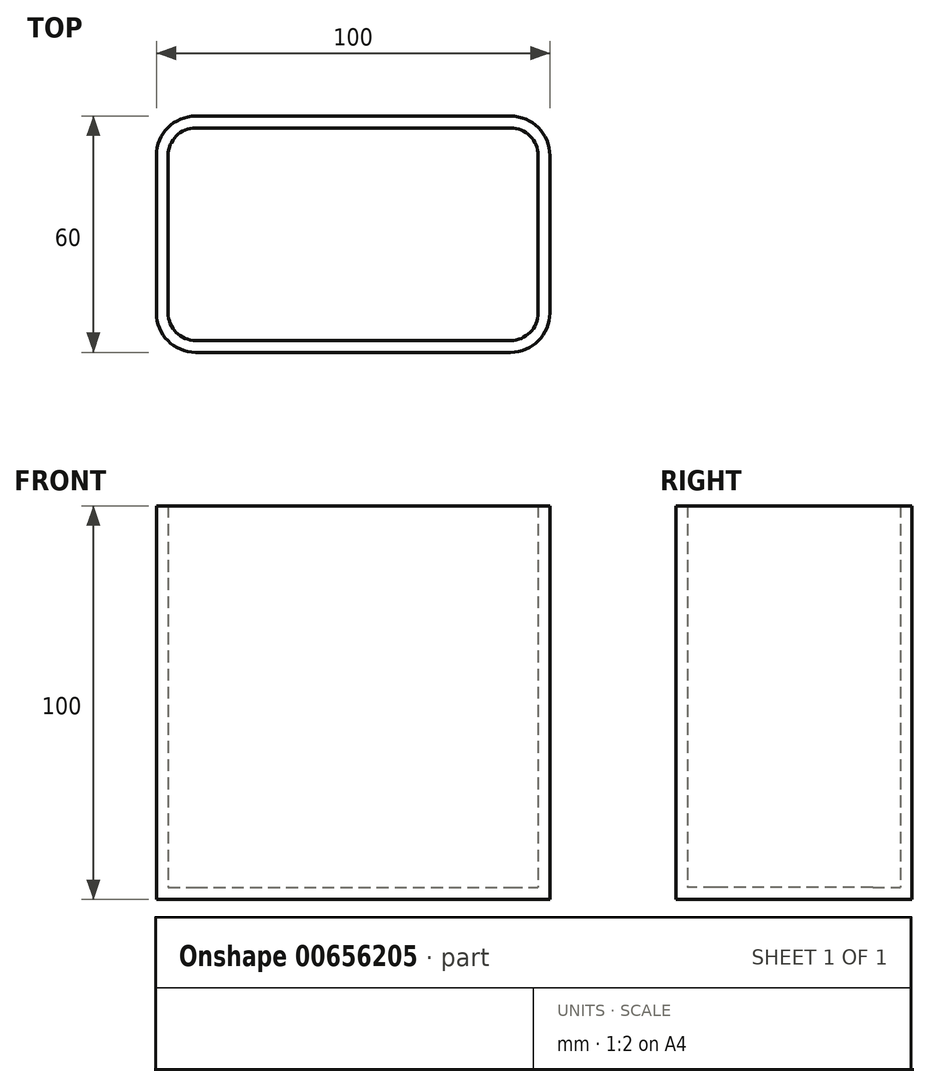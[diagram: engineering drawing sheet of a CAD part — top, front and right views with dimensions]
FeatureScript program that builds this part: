
annotation { "Feature Type Name" : "Feature", "Feature Type Description" : "" }
export const myFeature = defineFeature(function(context is Context, id is Id, definition is map)
    precondition{}
    {
        {
            var Q0;
            Q0=qCreatedBy(makeId("Top.planeOp"),FACE);
            var sketch = newSketch(context, id + "F0", { "sketchPlane" : qUnion([Q0])});
            skLineSegment(sketch, "E0.bottom", {"start": v(40, 30) * mm, "end": v(-40, 30) * mm});
            skLineSegment(sketch, "E0.top", {"start": v(40, -30) * mm, "end": v(-40, -30) * mm});
            skLineSegment(sketch, "E0.left", {"start": v(50, 20) * mm, "end": v(50, -20) * mm});
            skLineSegment(sketch, "E0.right", {"start": v(-50, 20) * mm, "end": v(-50, -20) * mm});
            skPoint(sketch, "E0.middle", {"position": v(0, 0) * mm});
            skPoint(sketch, "E1.visualSharp", {"position": v(-50, 30) * mm});
            skArc(sketch, "E1.filletArc", {"start": v(-40, 30) * mm, "mid": v(-47.07, 27.07) * mm, "end": v(-50, 20) * mm});
            skPoint(sketch, "E2.visualSharp", {"position": v(50, 30) * mm});
            skArc(sketch, "E2.filletArc", {"start": v(50, 20) * mm, "mid": v(47.07, 27.07) * mm, "end": v(40, 30) * mm});
            skPoint(sketch, "E3.visualSharp", {"position": v(50, -30) * mm});
            skArc(sketch, "E3.filletArc", {"start": v(40, -30) * mm, "mid": v(47.07, -27.07) * mm, "end": v(50, -20) * mm});
            skPoint(sketch, "E4.visualSharp", {"position": v(-50, -30) * mm});
            skArc(sketch, "E4.filletArc", {"start": v(-50, -20) * mm, "mid": v(-47.07, -27.07) * mm, "end": v(-40, -30) * mm});
            skSolve(sketch);
        }
        {
            var Q0;
            Q0 = qSketchRegion(id + "F0", true);
            extrude(context, id + "F1", {"entities" : qUnion([Q0]), "depth" : 3 * mm, "offsetDistance" : 25 * mm});
        }
        {
            var Q0;
            Q0=makeQuery(id+"F1.opExtrude","CAP_FACE",FACE,{"disambiguationData":[OSD([sQuery(id+"F0.wireOp",EDGE,"E0.bottom"),sQuery(id+"F0.wireOp",EDGE,"E0.top"),sQuery(id+"F0.wireOp",EDGE,"E0.left"),sQuery(id+"F0.wireOp",EDGE,"E0.right"),sQuery(id+"F0.wireOp",EDGE,"E1.filletArc"),sQuery(id+"F0.wireOp",EDGE,"E2.filletArc"),sQuery(id+"F0.wireOp",EDGE,"E3.filletArc"),sQuery(id+"F0.wireOp",EDGE,"E4.filletArc")])],"isStart":false});
            var sketch = newSketch(context, id + "F2", { "sketchPlane" : qUnion([Q0])});
            skArc(sketch, "E5.0", {"start": v(-47, -20) * mm, "mid": v(-44.95, -24.95) * mm, "end": v(-40, -27) * mm});
            skLineSegment(sketch, "E5.1", {"start": v(-47, 20) * mm, "end": v(-47, -20) * mm});
            skLineSegment(sketch, "E5.2", {"start": v(-40, -27) * mm, "end": v(40, -27) * mm});
            skArc(sketch, "E5.3", {"start": v(-40, 27) * mm, "mid": v(-44.95, 24.95) * mm, "end": v(-47, 20) * mm});
            skArc(sketch, "E5.4", {"start": v(40, -27) * mm, "mid": v(44.95, -24.95) * mm, "end": v(47, -20) * mm});
            skLineSegment(sketch, "E5.5", {"start": v(47, -20) * mm, "end": v(47, 20) * mm});
            skArc(sketch, "E5.6", {"start": v(47, 20) * mm, "mid": v(44.95, 24.95) * mm, "end": v(40, 27) * mm});
            skLineSegment(sketch, "E5.7", {"start": v(40, 27) * mm, "end": v(-40, 27) * mm});
            skSolve(sketch);
        }
        {
            var Q0;
            Q0 = qSketchRegion(id + "F0", true);
            extrude(context, id + "F3", {"entities" : qUnion([Q0]), "operationType" : NewBodyOperationType.ADD, "depth" : 100 * mm, "offsetDistance" : 25 * mm});
        }
        {
            var Q0;
            Q0 = qSketchRegion(id + "F2", true);
            extrude(context, id + "F4", {"entities" : qUnion([Q0]), "operationType" : NewBodyOperationType.REMOVE, "depth" : 100 * mm, "offsetDistance" : 25 * mm});
        }
    });
